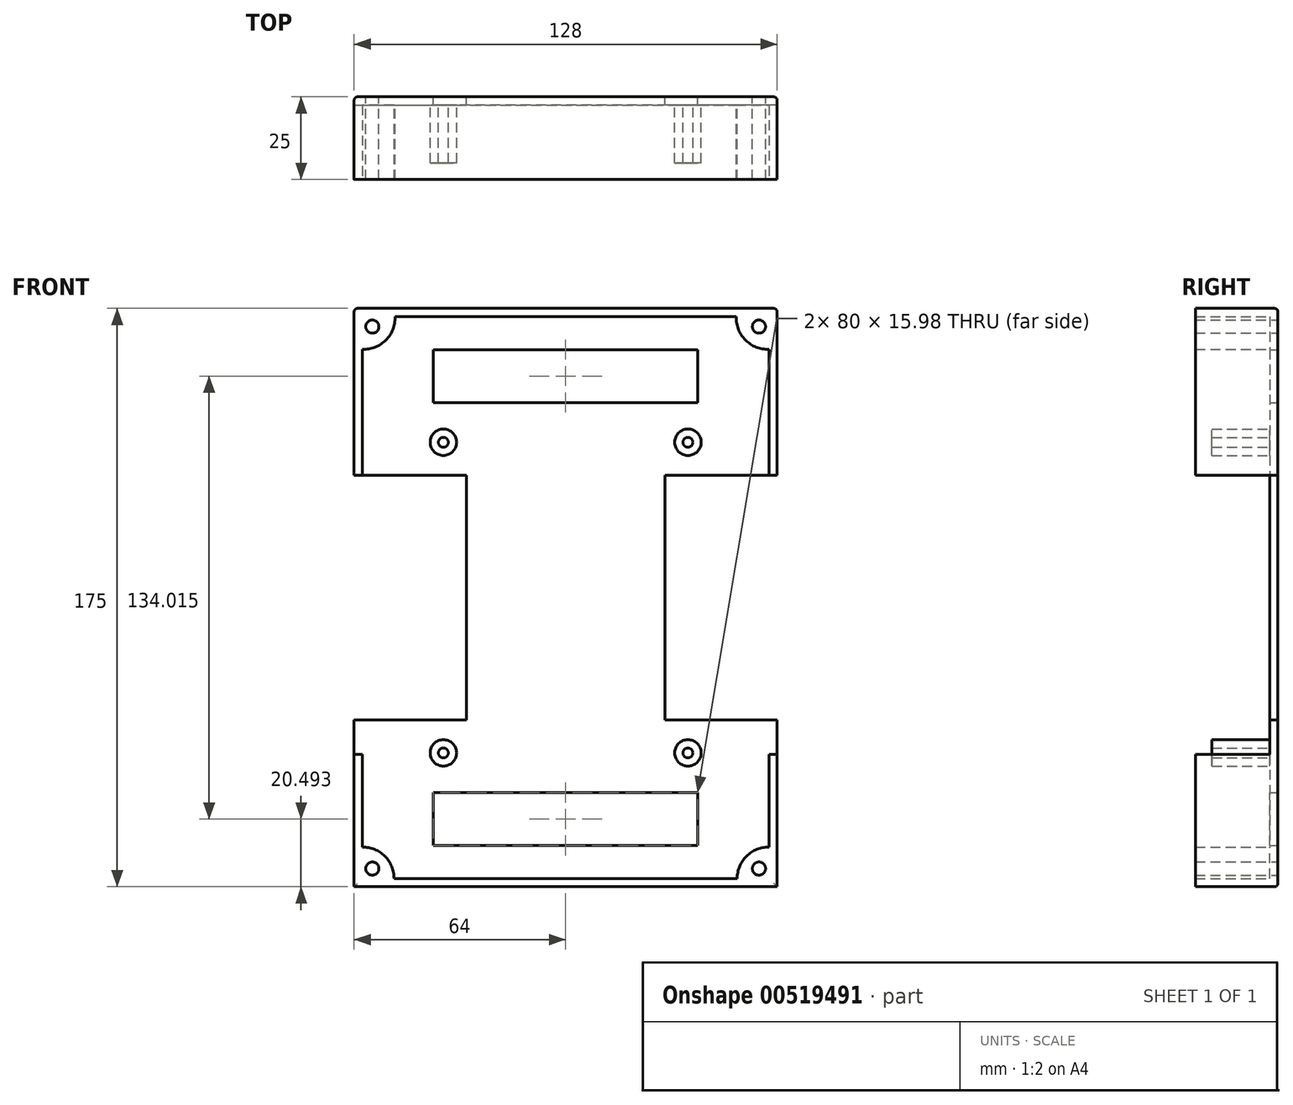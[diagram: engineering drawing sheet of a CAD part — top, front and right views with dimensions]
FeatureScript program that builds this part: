
annotation { "Feature Type Name" : "Feature", "Feature Type Description" : "" }
export const myFeature = defineFeature(function(context is Context, id is Id, definition is map)
    precondition{}
    {
        {
            var Q0;
            Q0=qCreatedBy(makeId("Front.planeOp"),FACE);
            var sketch = newSketch(context, id + "F0", { "sketchPlane" : qUnion([Q0])});
            skLineSegment(sketch, "E0.bottom", {"start": v(-64, 87.5) * mm, "end": v(64, 87.5) * mm});
            skLineSegment(sketch, "E0.top", {"start": v(-64, -87.5) * mm, "end": v(64, -87.5) * mm});
            skLineSegment(sketch, "E0.left", {"start": v(-64, 87.5) * mm, "end": v(-64, -87.5) * mm});
            skLineSegment(sketch, "E0.right", {"start": v(64, 87.5) * mm, "end": v(64, -87.5) * mm});
            skPoint(sketch, "E0.middle", {"position": v(0, 0) * mm});
            skSolve(sketch);
        }
        {
            var Q0;
            Q0=qSketchRegion(id+"F0",true);
            extrude(context, id + "F1", {"entities" : qUnion([Q0]), "depth" : 25 * mm, "offsetDistance" : 25 * mm});
        }
        {
            var Q0;
            Q0=makeQuery(id+"F1.opExtrude","CAP_FACE",FACE,{"disambiguationData":[OSD([sQuery(id+"F0.wireOp",EDGE,"E0.bottom"),sQuery(id+"F0.wireOp",EDGE,"E0.top"),sQuery(id+"F0.wireOp",EDGE,"E0.left"),sQuery(id+"F0.wireOp",EDGE,"E0.right")])],"isStart":false});
            shell(context, id + "F2", {"entities" : qUnion([Q0]), "thickness" : 2.5 * mm});
        }
        {
            var Q0;
            Q0=qCreatedBy(makeId("Front.planeOp"),FACE);
            var sketch = newSketch(context, id + "F3", { "sketchPlane" : qUnion([Q0])});
            skCircle(sketch, "E1", {"center": v(-37, 47) * mm, "radius": 4 * mm});
            skCircle(sketch, "E2.MirrorC", {"center": v(37, 47) * mm, "radius": 4 * mm});
            skCircle(sketch, "E3.MirrorC", {"center": v(37, -47) * mm, "radius": 4 * mm});
            skCircle(sketch, "E4.MirrorC", {"center": v(-37, -47) * mm, "radius": 4 * mm});
            skCircle(sketch, "E5", {"center": v(-37, 47) * mm, "radius": 1.5 * mm});
            skCircle(sketch, "E6", {"center": v(37, 47) * mm, "radius": 1.5 * mm});
            skCircle(sketch, "E7", {"center": v(-37, -47) * mm, "radius": 1.5 * mm});
            skCircle(sketch, "E8", {"center": v(37, -47) * mm, "radius": 1.5 * mm});
            skSolve(sketch);
        }
        {
            var Q0;
            Q0=qSketchRegion(id+"F3",true);
            extrude(context, id + "F4", {"entities" : qUnion([Q0]), "operationType" : NewBodyOperationType.ADD, "depth" : 20 * mm, "offsetDistance" : 25 * mm});
        }
        {
            var Q0;
            Q0=qCreatedBy(makeId("Front.planeOp"),FACE);
            cPlane(context, id + "F5", {"entities" : qUnion([Q0]), "cplaneType" : CPlaneType.OFFSET, "offset" : 3 * mm, "width" : 150 * mm, "height" : 150 * mm});
        }
        {
            var Q0;
            Q0=qCreatedBy(makeId("Front.planeOp"),FACE);
            var sketch = newSketch(context, id + "F6", { "sketchPlane" : qUnion([Q0])});
            skLineSegment(sketch, "E9.bottom", {"start": v(-61.93, -85.52) * mm, "end": v(-61.93, -75.52) * mm});
            skLineSegment(sketch, "E9.left", {"start": v(-61.93, -85.52) * mm, "end": v(-51.93, -85.52) * mm});
            skArc(sketch, "E10", {"start": v(-51.93, -85.52) * mm, "mid": v(-54.7, -78.28) * mm, "end": v(-61.93, -75.52) * mm});
            skArc(sketch, "E11.MirrorCS", {"start": v(51.93, -85.52) * mm, "mid": v(54.7, -78.28) * mm, "end": v(61.93, -75.52) * mm});
            skLineSegment(sketch, "E12.MirrorCS", {"start": v(61.93, -85.52) * mm, "end": v(51.93, -85.52) * mm});
            skLineSegment(sketch, "E13.MirrorCS", {"start": v(61.93, -85.52) * mm, "end": v(61.93, -75.52) * mm});
            skArc(sketch, "E14.MirrorCS", {"start": v(-51.64, 85.15) * mm, "mid": v(-54.4, 77.91) * mm, "end": v(-61.64, 75.15) * mm});
            skLineSegment(sketch, "E15.MirrorCS", {"start": v(-61.64, 85.15) * mm, "end": v(-51.64, 85.15) * mm});
            skLineSegment(sketch, "E16.MirrorCS", {"start": v(-61.64, 85.15) * mm, "end": v(-61.64, 75.15) * mm});
            skLineSegment(sketch, "E17.MirrorCS", {"start": v(61.64, 85.15) * mm, "end": v(51.64, 85.15) * mm});
            skLineSegment(sketch, "E18.MirrorCS", {"start": v(61.64, 85.15) * mm, "end": v(61.64, 75.15) * mm});
            skArc(sketch, "E19.MirrorCS", {"start": v(51.64, 85.15) * mm, "mid": v(54.4, 77.91) * mm, "end": v(61.64, 75.15) * mm});
            skSolve(sketch);
        }
        {
            var Q0;
            Q0=qSketchRegion(id+"F6",true);
            extrude(context, id + "F7", {"entities" : qUnion([Q0]), "operationType" : NewBodyOperationType.ADD, "depth" : 25 * mm, "offsetDistance" : 25 * mm});
        }
        {
            var Q0;
            Q0=qCreatedBy(makeId("Front.planeOp"),FACE);
            var sketch = newSketch(context, id + "F8", { "sketchPlane" : qUnion([Q0])});
            skCircle(sketch, "E20", {"center": v(-58.5, 82) * mm, "radius": 2 * mm});
            skCircle(sketch, "E21", {"center": v(-58.5, -82) * mm, "radius": 2 * mm});
            skCircle(sketch, "E22.MirrorC", {"center": v(58.5, -82) * mm, "radius": 2 * mm});
            skCircle(sketch, "E23.MirrorC", {"center": v(58.5, 82) * mm, "radius": 2 * mm});
            skSolve(sketch);
        }
        {
            var Q0;
            Q0 = qSketchRegion(id + "F8", true);
            extrude(context, id + "F9", {"entities" : qUnion([Q0]), "operationType" : NewBodyOperationType.REMOVE, "depth" : 25 * mm, "offsetDistance" : 25 * mm});
        }
        {
            var Q0;
            Q0=qCreatedBy(makeId("Front.planeOp"),FACE);
            cPlane(context, id + "F10", {"entities" : qUnion([Q0]), "cplaneType" : CPlaneType.OFFSET, "offset" : 10 * mm, "oppositeDirection" : true, "width" : 150 * mm, "height" : 150 * mm});
        }
        {
            var Q0;
            Q0=qCreatedBy(id+"F10.planeOp",FACE);
            var sketch = newSketch(context, id + "F11", { "sketchPlane" : qUnion([Q0])});
            skLineSegment(sketch, "E24.bottom", {"start": v(-30, 37) * mm, "end": v(-70, 37) * mm});
            skLineSegment(sketch, "E24.top", {"start": v(-30, -37) * mm, "end": v(-70, -37) * mm});
            skLineSegment(sketch, "E24.left", {"start": v(-30, 37) * mm, "end": v(-30, -37) * mm});
            skLineSegment(sketch, "E24.right", {"start": v(-70, 37) * mm, "end": v(-70, -37) * mm});
            skLineSegment(sketch, "E25.MirrorCS", {"start": v(30, 37) * mm, "end": v(70, 37) * mm});
            skLineSegment(sketch, "E26.MirrorCS", {"start": v(70, 37) * mm, "end": v(70, -37) * mm});
            skLineSegment(sketch, "E27.MirrorCS", {"start": v(30, -37) * mm, "end": v(70, -37) * mm});
            skLineSegment(sketch, "E28.MirrorCS", {"start": v(30, 37) * mm, "end": v(30, -37) * mm});
            skLineSegment(sketch, "E29.bottom", {"start": v(-40, 59.01) * mm, "end": v(40, 59.01) * mm});
            skLineSegment(sketch, "E29.top", {"start": v(-40, 75) * mm, "end": v(40, 75) * mm});
            skLineSegment(sketch, "E29.left", {"start": v(-40, 59.01) * mm, "end": v(-40, 75) * mm});
            skLineSegment(sketch, "E29.right", {"start": v(40, 59.01) * mm, "end": v(40, 75) * mm});
            skLineSegment(sketch, "E30.MirrorCS", {"start": v(-40, -75) * mm, "end": v(40, -75) * mm});
            skLineSegment(sketch, "E31.MirrorCS", {"start": v(40, -59.01) * mm, "end": v(40, -75) * mm});
            skLineSegment(sketch, "E32.MirrorCS", {"start": v(-40, -59.01) * mm, "end": v(40, -59.01) * mm});
            skLineSegment(sketch, "E33.MirrorCS", {"start": v(-40, -59.01) * mm, "end": v(-40, -75) * mm});
            skSolve(sketch);
        }
        {
            var Q0;
            Q0 = qSketchRegion(id + "F11", true);
            extrude(context, id + "F12", {"entities" : qUnion([Q0]), "operationType" : NewBodyOperationType.REMOVE, "depth" : 36 * mm, "offsetDistance" : 25 * mm});
        }
        {
            var Q0;
            Q0=makeQuery(id+"F1.opExtrude","SWEPT_EDGE",EDGE,{"disambiguationData":[OSD([sQuery(id+"F0.wireOp",EDGE,"E0.bottom"),sQuery(id+"F0.wireOp",EDGE,"E0.right")])]});
            var Q1;
            Q1=makeQuery(id+"F1.opExtrude","CAP_EDGE",EDGE,{"disambiguationData":[OSD([sQuery(id+"F0.wireOp",EDGE,"E0.bottom")])],"isStart":true});
            var Q2;
            {var subQ0=sQuery(id+"F0.wireOp",EDGE,"E0.bottom");var subQ1=sQuery(id+"F0.wireOp",EDGE,"E0.right");Q2=makeQuery(id+"F12.boolean.opBoolean","SPLIT",EDGE,{"disambiguationData":[TD([makeQuery(id+"F1.opExtrude","SWEPT_FACE",FACE,{"disambiguationData":[OSD([subQ0])]})])],"derivedFrom":makeQuery(id+"F1.opExtrude","CAP_EDGE",EDGE,{"disambiguationData":[OSD([subQ1])],"isStart":true})});}
            var Q3;
            {var subQ0=sQuery(id+"F0.wireOp",EDGE,"E0.right");var subQ1=sQuery(id+"F0.wireOp",EDGE,"E0.top");Q3=makeQuery(id+"F12.boolean.opBoolean","SPLIT",EDGE,{"disambiguationData":[TD([makeQuery(id+"F1.opExtrude","SWEPT_FACE",FACE,{"disambiguationData":[OSD([subQ1])]})])],"derivedFrom":makeQuery(id+"F1.opExtrude","CAP_EDGE",EDGE,{"disambiguationData":[OSD([subQ0])],"isStart":true})});}
            var Q4;
            Q4=makeQuery(id+"F1.opExtrude","CAP_EDGE",EDGE,{"disambiguationData":[OSD([sQuery(id+"F0.wireOp",EDGE,"E0.top")])],"isStart":true});
            var Q5;
            {var subQ0=sQuery(id+"F0.wireOp",EDGE,"E0.left");var subQ1=sQuery(id+"F0.wireOp",EDGE,"E0.top");Q5=makeQuery(id+"F12.boolean.opBoolean","SPLIT",EDGE,{"disambiguationData":[TD([makeQuery(id+"F1.opExtrude","SWEPT_FACE",FACE,{"disambiguationData":[OSD([subQ1])]})])],"derivedFrom":makeQuery(id+"F1.opExtrude","CAP_EDGE",EDGE,{"disambiguationData":[OSD([subQ0])],"isStart":true})});}
            var Q6;
            {var subQ0=sQuery(id+"F0.wireOp",EDGE,"E0.bottom");var subQ1=sQuery(id+"F0.wireOp",EDGE,"E0.left");Q6=makeQuery(id+"F12.boolean.opBoolean","SPLIT",EDGE,{"disambiguationData":[TD([makeQuery(id+"F1.opExtrude","SWEPT_FACE",FACE,{"disambiguationData":[OSD([subQ0])]})])],"derivedFrom":makeQuery(id+"F1.opExtrude","CAP_EDGE",EDGE,{"disambiguationData":[OSD([subQ1])],"isStart":true})});}
            var Q7;
            Q7=makeQuery(id+"F1.opExtrude","SWEPT_EDGE",EDGE,{"disambiguationData":[OSD([sQuery(id+"F0.wireOp",EDGE,"E0.bottom"),sQuery(id+"F0.wireOp",EDGE,"E0.left")])]});
            fillet(context, id + "F13", {"entities" : qUnion([Q0, Q1, Q2, Q3, Q4, Q5, Q6, Q7]), "radius" : 1 * mm, "tangentPropagation" : true, "allowEdgeOverflow" : false});
        }
        {
            var Q0;
            Q0=qCreatedBy(makeId("Front.planeOp"),FACE);
            cPlane(context, id + "F14", {"entities" : qUnion([Q0]), "cplaneType" : CPlaneType.OFFSET, "offset" : 25 * mm, "width" : 150 * mm, "height" : 150 * mm});
        }
        {
            var Q0;
            Q0=qCreatedBy(makeId("Top.planeOp"),FACE);
            var sketch = newSketch(context, id + "F15", { "sketchPlane" : qUnion([Q0])});
            skLineSegment(sketch, "E34.bottom", {"start": v(-65.66, -27.92) * mm, "end": v(-60.58, -27.92) * mm});
            skLineSegment(sketch, "E34.top", {"start": v(-65.66, -2.5) * mm, "end": v(-60.58, -2.5) * mm});
            skLineSegment(sketch, "E34.left", {"start": v(-65.66, -27.92) * mm, "end": v(-65.66, -2.5) * mm});
            skLineSegment(sketch, "E34.right", {"start": v(-60.58, -27.92) * mm, "end": v(-60.58, -2.5) * mm});
            skLineSegment(sketch, "E35.MirrorCS", {"start": v(65.66, -2.5) * mm, "end": v(60.58, -2.5) * mm});
            skLineSegment(sketch, "E36.MirrorCS", {"start": v(60.58, -27.92) * mm, "end": v(60.58, -2.5) * mm});
            skLineSegment(sketch, "E37.MirrorCS", {"start": v(65.66, -27.92) * mm, "end": v(65.66, -2.5) * mm});
            skLineSegment(sketch, "E38.MirrorCS", {"start": v(65.66, -27.92) * mm, "end": v(60.58, -27.92) * mm});
            skSolve(sketch);
        }
        {
            var Q0;
            Q0 = qSketchRegion(id + "F15", true);
            extrude(context, id + "F16", {"entities" : qUnion([Q0]), "operationType" : NewBodyOperationType.REMOVE, "oppositeDirection" : true, "depth" : 47.5 * mm, "offsetDistance" : 25 * mm});
        }
    });
